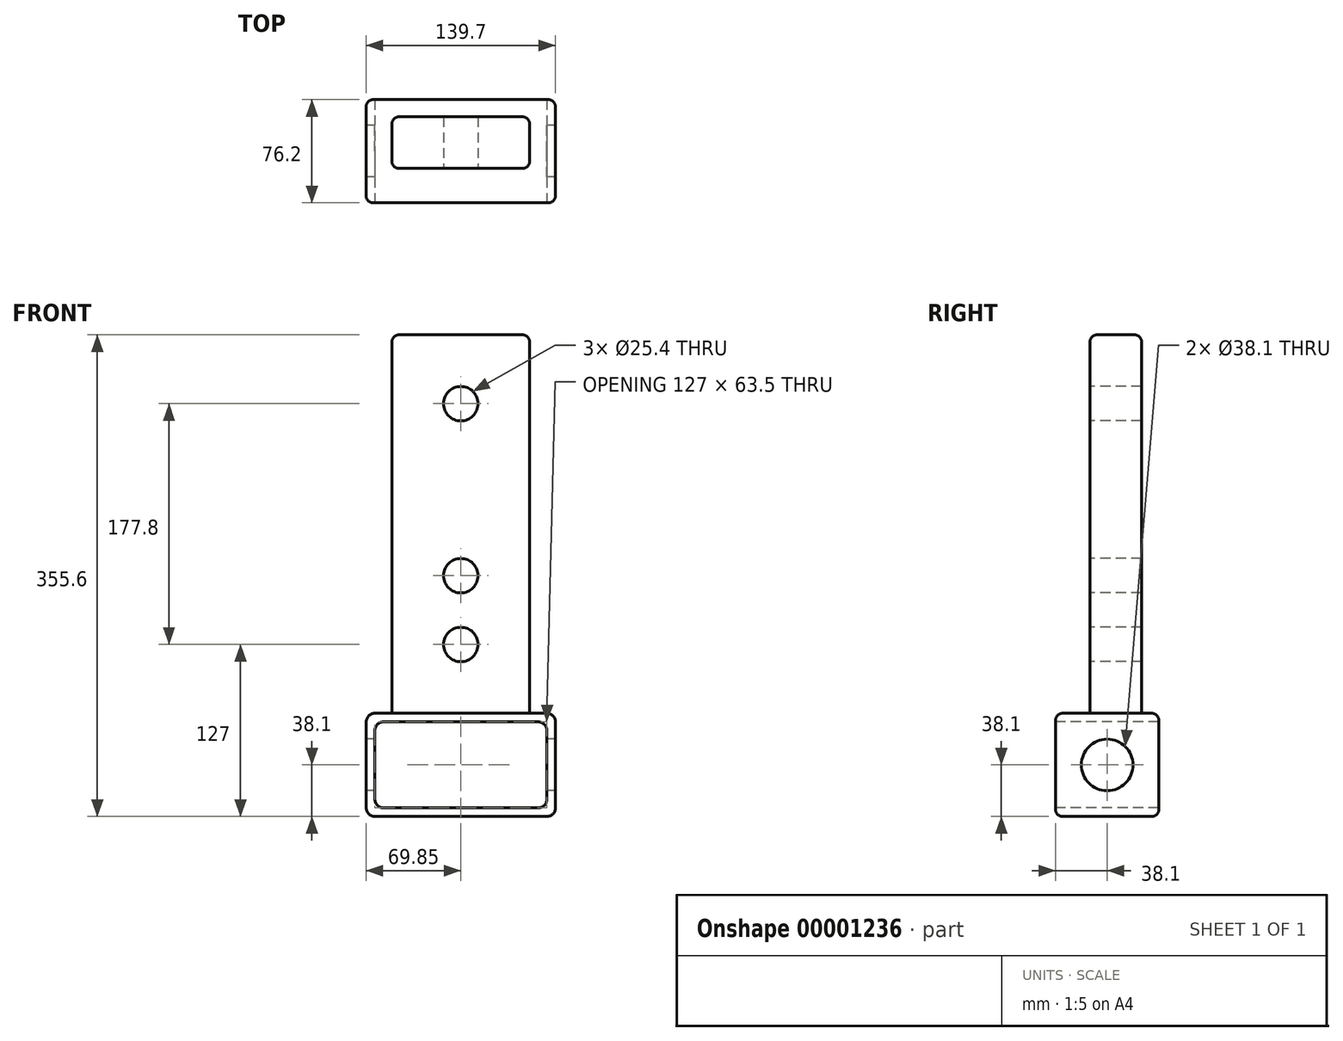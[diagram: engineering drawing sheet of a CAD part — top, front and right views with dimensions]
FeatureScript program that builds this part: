
annotation { "Feature Type Name" : "Feature", "Feature Type Description" : "" }
export const myFeature = defineFeature(function(context is Context, id is Id, definition is map)
    precondition{}
    {
        {
            var Q0;
            Q0=qCreatedBy(makeId("Front.planeOp"),FACE);
            var sketch = newSketch(context, id + "F0", { "sketchPlane" : qUnion([Q0])});
            skLineSegment(sketch, "E0.bottom", {"start": v(0, 0) * mm, "end": v(-127, 0) * mm});
            skLineSegment(sketch, "E0.top", {"start": v(0, 63.5) * mm, "end": v(-127, 63.5) * mm});
            skLineSegment(sketch, "E0.left", {"start": v(0, 0) * mm, "end": v(0, 63.5) * mm});
            skLineSegment(sketch, "E0.right", {"start": v(-127, 0) * mm, "end": v(-127, 63.5) * mm});
            skLineSegment(sketch, "E1.0", {"start": v(-133.35, -6.35) * mm, "end": v(-133.35, 69.85) * mm});
            skLineSegment(sketch, "E1.1", {"start": v(6.35, -6.35) * mm, "end": v(-133.35, -6.35) * mm});
            skLineSegment(sketch, "E1.2", {"start": v(6.35, -6.35) * mm, "end": v(6.35, 69.85) * mm});
            skLineSegment(sketch, "E1.3", {"start": v(6.35, 69.85) * mm, "end": v(-133.35, 69.85) * mm});
            skSolve(sketch);
        }
        {
            var Q0;
            Q0=makeQuery(id+"F0.imprint","IMPRINT",FACE,{"disambiguationData":[TD([[makeQuery(id+"F0.imprint","IMPRINT",EDGE,{"derivedFrom":sQuery(id+"F0.wireOp",EDGE,"E0.bottom")}),1.0]])]});
            extrude(context, id + "F1", {"entities" : qUnion([Q0]), "oppositeDirection" : true, "depth" : 76.2 * mm});
        }
        {
            var Q0;
            Q0=makeQuery(id+"F1.opExtrude","SWEPT_EDGE",EDGE,{"disambiguationData":[OSD([sQuery(id+"F0.wireOp",EDGE,"E1.0"),sQuery(id+"F0.wireOp",EDGE,"E1.3")])]});
            var Q1;
            Q1=makeQuery(id+"F1.opExtrude","SWEPT_EDGE",EDGE,{"disambiguationData":[OSD([sQuery(id+"F0.wireOp",EDGE,"E1.2"),sQuery(id+"F0.wireOp",EDGE,"E1.3")])]});
            var Q2;
            Q2=makeQuery(id+"F1.opExtrude","SWEPT_EDGE",EDGE,{"disambiguationData":[OSD([sQuery(id+"F0.wireOp",EDGE,"E0.bottom"),sQuery(id+"F0.wireOp",EDGE,"E0.left")])]});
            var Q3;
            Q3=makeQuery(id+"F1.opExtrude","SWEPT_EDGE",EDGE,{"disambiguationData":[OSD([sQuery(id+"F0.wireOp",EDGE,"E1.0"),sQuery(id+"F0.wireOp",EDGE,"E1.1")])]});
            var Q4;
            Q4=makeQuery(id+"F1.opExtrude","SWEPT_EDGE",EDGE,{"disambiguationData":[OSD([sQuery(id+"F0.wireOp",EDGE,"E0.top"),sQuery(id+"F0.wireOp",EDGE,"E0.right")])]});
            var Q5;
            Q5=makeQuery(id+"F1.opExtrude","SWEPT_EDGE",EDGE,{"disambiguationData":[OSD([sQuery(id+"F0.wireOp",EDGE,"E0.top"),sQuery(id+"F0.wireOp",EDGE,"E0.left")])]});
            var Q6;
            Q6=makeQuery(id+"F1.opExtrude","SWEPT_EDGE",EDGE,{"disambiguationData":[OSD([sQuery(id+"F0.wireOp",EDGE,"E0.bottom"),sQuery(id+"F0.wireOp",EDGE,"E0.right")])]});
            var Q7;
            Q7=makeQuery(id+"F1.opExtrude","SWEPT_EDGE",EDGE,{"disambiguationData":[OSD([sQuery(id+"F0.wireOp",EDGE,"E1.1"),sQuery(id+"F0.wireOp",EDGE,"E1.2")])]});
            fillet(context, id + "F2", {"entities" : qUnion([Q0, Q1, Q2, Q3, Q4, Q5, Q6, Q7]), "radius" : 6.35 * mm, "tangentPropagation" : true, "allowEdgeOverflow" : false});
        }
        {
            var Q0;
            Q0=makeQuery(id+"F1.opExtrude","SWEPT_FACE",FACE,{"disambiguationData":[OSD([sQuery(id+"F0.wireOp",EDGE,"E1.0")])]});
            var sketch = newSketch(context, id + "F3", { "sketchPlane" : qUnion([Q0])});
            skCircle(sketch, "E2", {"center": v(-38.1, 31.75) * mm, "radius": 19.05 * mm});
            skSolve(sketch);
        }
        {
            var Q0;
            Q0 = qSketchRegion(id + "F3", true);
            extrude(context, id + "F4", {"entities" : qUnion([Q0]), "operationType" : NewBodyOperationType.REMOVE, "endBound" : BoundingType.THROUGH_ALL, "oppositeDirection" : true, "depth" : 25.4 * mm});
        }
        {
            var Q0;
            Q0=makeQuery(id+"F1.opExtrude","SWEPT_FACE",FACE,{"disambiguationData":[OSD([sQuery(id+"F0.wireOp",EDGE,"E1.3")])]});
            var sketch = newSketch(context, id + "F5", { "sketchPlane" : qUnion([Q0])});
            skLineSegment(sketch, "E3.bottom", {"start": v(-114.3, 25.4) * mm, "end": v(-12.7, 25.4) * mm});
            skLineSegment(sketch, "E3.top", {"start": v(-114.3, 63.5) * mm, "end": v(-12.7, 63.5) * mm});
            skLineSegment(sketch, "E3.left", {"start": v(-114.3, 25.4) * mm, "end": v(-114.3, 63.5) * mm});
            skLineSegment(sketch, "E3.right", {"start": v(-12.7, 25.4) * mm, "end": v(-12.7, 63.5) * mm});
            skSolve(sketch);
        }
        {
            var Q0;
            Q0=makeQuery(id+"F5.imprint","IMPRINT",FACE,{"disambiguationData":[TD([[makeQuery(id+"F5.imprint","IMPRINT",EDGE,{"derivedFrom":sQuery(id+"F5.wireOp",EDGE,"E3.bottom")}),1.0]])]});
            extrude(context, id + "F6", {"entities" : qUnion([Q0]), "operationType" : NewBodyOperationType.ADD, "depth" : 279.4 * mm});
        }
        {
            var Q0;
            Q0=makeQuery(id+"F6.opExtrude","SWEPT_FACE",FACE,{"disambiguationData":[OSD([sQuery(id+"F5.wireOp",EDGE,"E3.bottom")])]});
            var sketch = newSketch(context, id + "F9", { "sketchPlane" : qUnion([Q0])});
            skLineSegment(sketch, "E4.0", {"start": v(-12.7, 349.25) * mm, "end": v(-12.7, 69.85) * mm});
            skLineSegment(sketch, "E5.0", {"start": v(-114.3, 349.25) * mm, "end": v(-12.7, 349.25) * mm});
            skLineSegment(sketch, "E6.0", {"start": v(-114.3, 349.25) * mm, "end": v(-114.3, 69.85) * mm});
            skLineSegment(sketch, "E7.0", {"start": v(-114.3, 69.85) * mm, "end": v(-12.7, 69.85) * mm});
            skCircle(sketch, "E8", {"center": v(-63.5, 298.45) * mm, "radius": 12.7 * mm});
            skCircle(sketch, "E9", {"center": v(-63.5, 171.45) * mm, "radius": 12.7 * mm});
            skCircle(sketch, "E10", {"center": v(-63.5, 120.65) * mm, "radius": 12.7 * mm});
            skSolve(sketch);
        }
        {
            var Q0;
            Q0=makeQuery(id+"F9.imprint","IMPRINT",FACE,{"disambiguationData":[TD([[makeQuery(id+"F9.imprint","IMPRINT",EDGE,{"derivedFrom":sQuery(id+"F9.wireOp",EDGE,"E8")}),1.0]])]});
            var Q1;
            Q1=makeQuery(id+"F9.imprint","IMPRINT",FACE,{"disambiguationData":[TD([[makeQuery(id+"F9.imprint","IMPRINT",EDGE,{"derivedFrom":sQuery(id+"F9.wireOp",EDGE,"E9")}),1.0]])]});
            var Q2;
            Q2=makeQuery(id+"F9.imprint","IMPRINT",FACE,{"disambiguationData":[TD([[makeQuery(id+"F9.imprint","IMPRINT",EDGE,{"derivedFrom":sQuery(id+"F9.wireOp",EDGE,"E10")}),1.0]])]});
            extrude(context, id + "F7", {"entities" : qUnion([Q0, Q1, Q2]), "operationType" : NewBodyOperationType.REMOVE, "endBound" : BoundingType.THROUGH_ALL, "oppositeDirection" : true, "depth" : 25.4 * mm});
        }
        {
            var Q0;
            Q0=makeQuery(id+"F6.opExtrude","SWEPT_EDGE",EDGE,{"disambiguationData":[OSD([sQuery(id+"F5.wireOp",EDGE,"E3.bottom"),sQuery(id+"F5.wireOp",EDGE,"E3.right")])]});
            var Q1;
            Q1=makeQuery(id+"F6.opExtrude","SWEPT_EDGE",EDGE,{"disambiguationData":[OSD([sQuery(id+"F5.wireOp",EDGE,"E3.bottom"),sQuery(id+"F5.wireOp",EDGE,"E3.left")])]});
            var Q2;
            Q2=makeQuery(id+"F6.opExtrude","CAP_EDGE",EDGE,{"disambiguationData":[OSD([sQuery(id+"F5.wireOp",EDGE,"E3.bottom")])],"isStart":false});
            var Q3;
            Q3=makeQuery(id+"F6.opExtrude","CAP_EDGE",EDGE,{"disambiguationData":[OSD([sQuery(id+"F5.wireOp",EDGE,"E3.top")])],"isStart":false});
            var Q4;
            Q4=makeQuery(id+"F6.opExtrude","SWEPT_EDGE",EDGE,{"disambiguationData":[OSD([sQuery(id+"F5.wireOp",EDGE,"E3.top"),sQuery(id+"F5.wireOp",EDGE,"E3.right")])]});
            var Q5;
            Q5=makeQuery(id+"F6.opExtrude","CAP_EDGE",EDGE,{"disambiguationData":[OSD([sQuery(id+"F5.wireOp",EDGE,"E3.right")])],"isStart":false});
            var Q6;
            Q6=makeQuery(id+"F6.opExtrude","CAP_EDGE",EDGE,{"disambiguationData":[OSD([sQuery(id+"F5.wireOp",EDGE,"E3.left")])],"isStart":false});
            var Q7;
            Q7=makeQuery(id+"F6.opExtrude","SWEPT_EDGE",EDGE,{"disambiguationData":[OSD([sQuery(id+"F5.wireOp",EDGE,"E3.top"),sQuery(id+"F5.wireOp",EDGE,"E3.left")])]});
            fillet(context, id + "F10", {"entities" : qUnion([Q0, Q1, Q2, Q3, Q4, Q5, Q6, Q7]), "radius" : 5.08 * mm, "tangentPropagation" : true, "allowEdgeOverflow" : false});
        }
        {
            var Q0;
            Q0=makeQuery(id+"F1.opExtrude","CAP_EDGE",EDGE,{"disambiguationData":[OSD([sQuery(id+"F0.wireOp",EDGE,"E1.3")])],"isStart":true});
            var Q1;
            Q1=makeQuery(id+"F1.opExtrude","CAP_EDGE",EDGE,{"disambiguationData":[OSD([sQuery(id+"F0.wireOp",EDGE,"E1.3")])],"isStart":false});
            fillet(context, id + "F8", {"entities" : qUnion([Q0, Q1]), "radius" : 5.08 * mm, "tangentPropagation" : true, "allowEdgeOverflow" : false});
        }
    });
